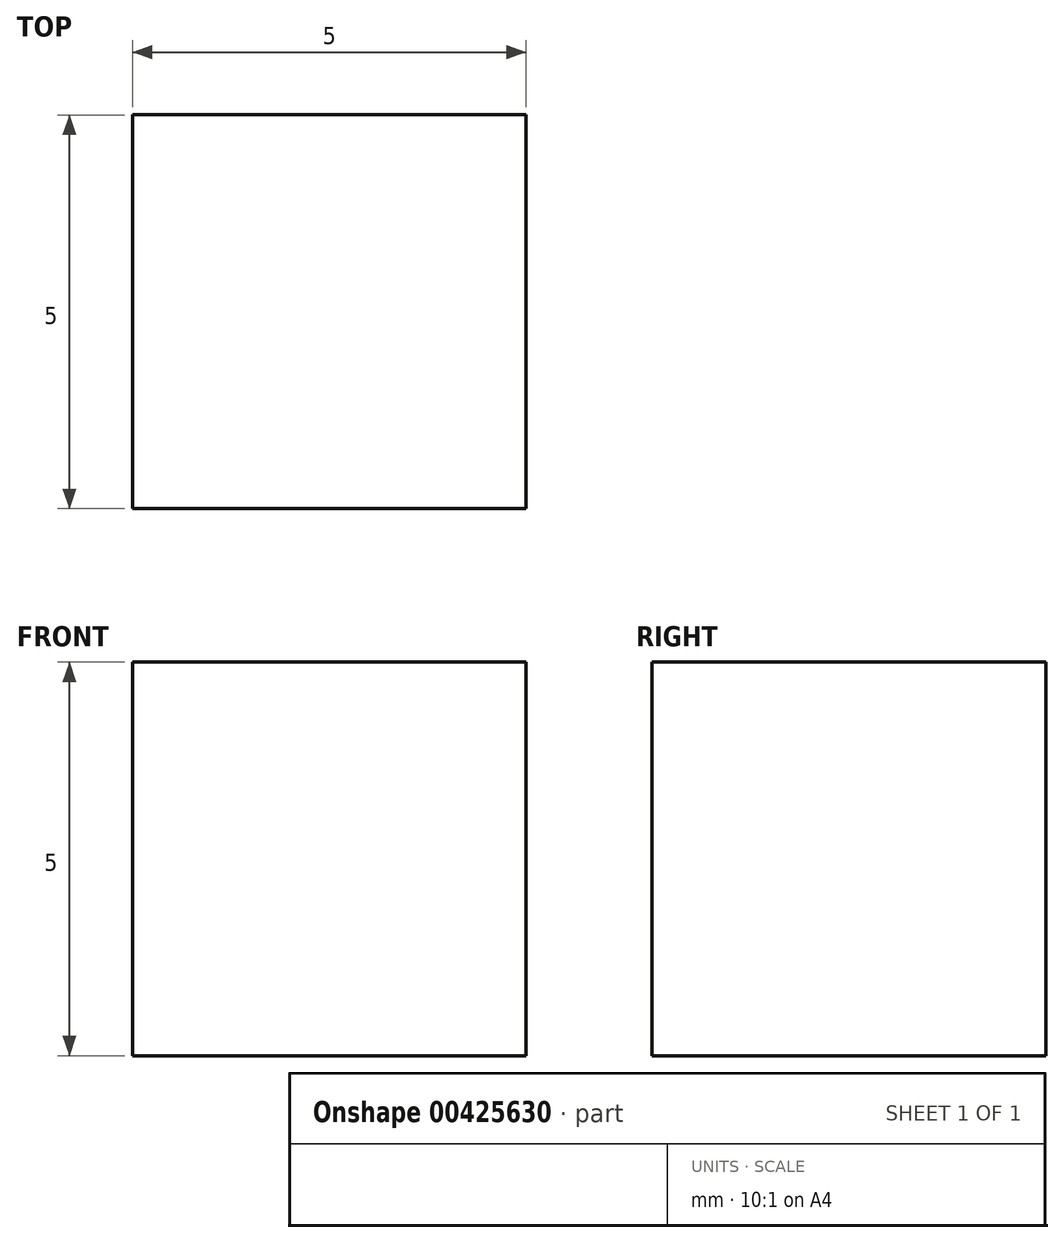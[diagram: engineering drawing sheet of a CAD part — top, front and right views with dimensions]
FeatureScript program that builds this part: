
annotation { "Feature Type Name" : "Feature", "Feature Type Description" : "" }
export const myFeature = defineFeature(function(context is Context, id is Id, definition is map)
    precondition{}
    {
        {
            var Q0;
            Q0=qCreatedBy(makeId("Top.planeOp"),FACE);
            var sketch = newSketch(context, id + "F0", { "sketchPlane" : qUnion([Q0])});
            skLineSegment(sketch, "E0.bottom", {"start": v(-5, 1.7) * mm, "end": v(0, 1.7) * mm});
            skLineSegment(sketch, "E0.top", {"start": v(-5, -3.3) * mm, "end": v(0, -3.3) * mm});
            skLineSegment(sketch, "E0.left", {"start": v(-5, 1.7) * mm, "end": v(-5, -3.3) * mm});
            skLineSegment(sketch, "E0.right", {"start": v(0, 1.7) * mm, "end": v(0, -3.3) * mm});
            skSolve(sketch);
        }
        {
            var Q0;
            Q0 = qSketchRegion(id + "F0", true);
            extrude(context, id + "F1", {"entities" : qUnion([Q0]), "depth" : 5 * mm});
        }
    });
